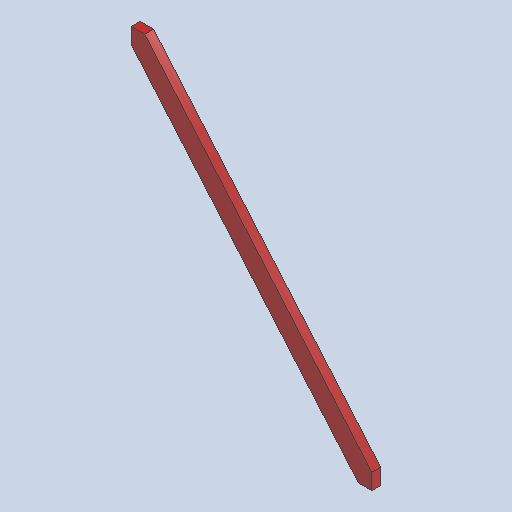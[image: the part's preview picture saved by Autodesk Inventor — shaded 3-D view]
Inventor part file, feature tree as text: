
AUTODESK INVENTOR PART (.ipt)
format: ipt  version: 2025.1 (Build 291241020, 241B)  size: 258,048 bytes
history: native  units: in
note: dims shown in document units (in); Inventor stores cm internally (conversion verified against a paired STEP export)
features: other x7, reference x4, extrude x1, sketch x1
ambient origin geometry x8: Origin, YZ Plane, XZ Plane, XY Plane, X Axis, Y Axis, Z Axis, Center Point
bodies: Solid1 (feature_tree)
feature tree (13):
  extrude  "Extrusion1"  [1 undecoded]
  sketch  "Sketch1"  dims[d2=1.5in d3=0.0in]
  reference  "Reference1"
  reference  "Reference2"
  reference  "Reference3"
  reference  "Reference4"
  other  "<userpath>\Documents\Tburn24\B_Legs0\B_Legs0.iam"
  other  "B_Legs0.iam"
  other  "4x2x4:1"
  other  "3'5x2x4:1"
  other  "4x2x4:2"
  other  "3'5x2x4:4"
  other  "Finish1"
note: 1 required parameter value undecoded (feature->parameter linkage not recoverable at this tier; creation-order binding heuristic only, values carry confidence <= 0.55)
